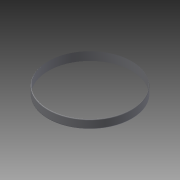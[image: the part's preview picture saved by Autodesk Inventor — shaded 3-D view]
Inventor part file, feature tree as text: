
AUTODESK INVENTOR PART (.ipt)
format: ipt  version: 2015 (Build 190159000, 159)  size: 86,016 bytes
history: native  units: in
note: dims shown in document units (in); Inventor stores cm internally (conversion verified against a paired STEP export)
features: fillet x2, extrude x1, sketch x1
ambient origin geometry x8: Origin, YZ Plane, XZ Plane, XY Plane, X Axis, Y Axis, Z Axis, Center Point
bodies: Solid1 (feature_tree)
feature tree (4):
  extrude  "Extrusion1"  Depth=0.125in
  fillet  "Fillet1"  Radius=1.0in
  fillet  "Fillet2"  Radius=0.125in
  sketch  "Sketch1"  dims[d0=9.9in d1=10.0in d2=1.0in d3=0.0in d4=0.125in d5=0.125in]
